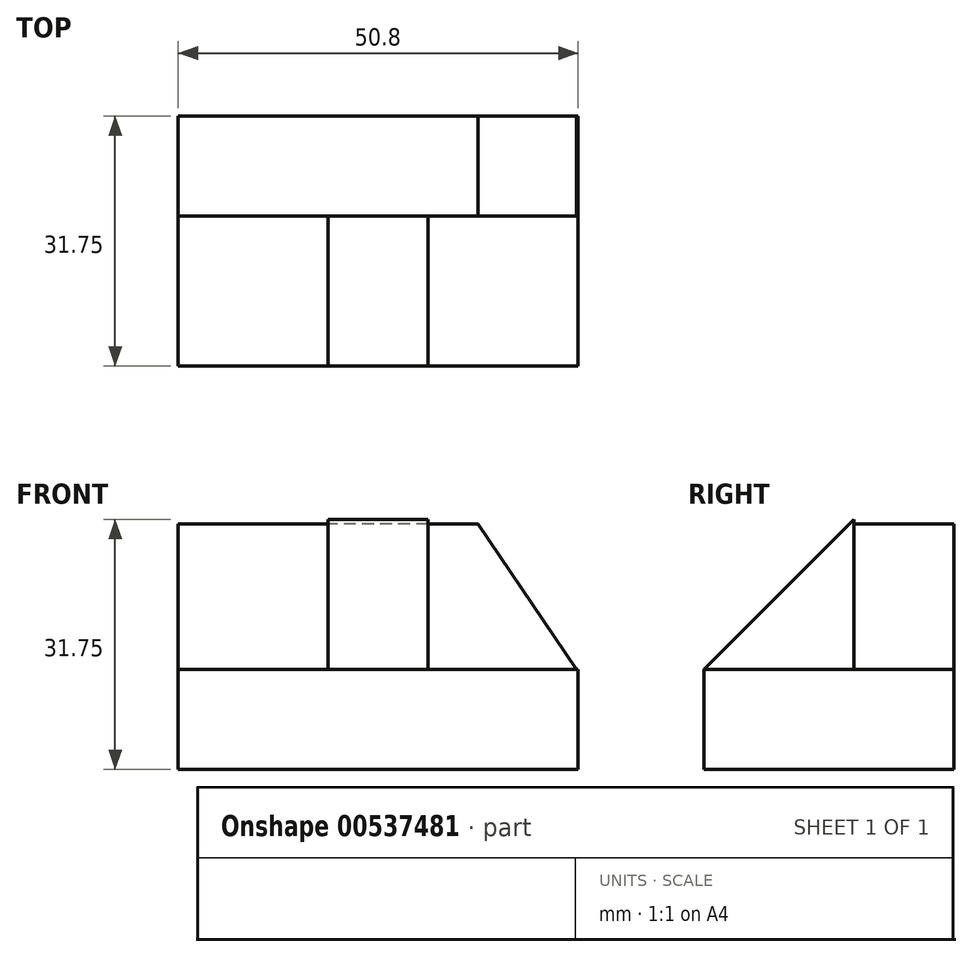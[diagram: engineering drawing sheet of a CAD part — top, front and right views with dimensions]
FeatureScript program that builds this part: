
annotation { "Feature Type Name" : "Feature", "Feature Type Description" : "" }
export const myFeature = defineFeature(function(context is Context, id is Id, definition is map)
    precondition{}
    {
        {
            var Q0;
            Q0=qCreatedBy(makeId("Front.planeOp"),FACE);
            var sketch = newSketch(context, id + "F0", { "sketchPlane" : qUnion([Q0])});
            skLineSegment(sketch, "E0", {"start": v(0, 0) * mm, "end": v(0, 31.75) * mm});
            skLineSegment(sketch, "E1", {"start": v(0, 31.75) * mm, "end": v(38.1, 31.75) * mm});
            skLineSegment(sketch, "E2", {"start": v(38.1, 31.75) * mm, "end": v(50.8, 12.7) * mm});
            skLineSegment(sketch, "E3", {"start": v(50.8, 12.7) * mm, "end": v(50.8, 0) * mm});
            skLineSegment(sketch, "E4", {"start": v(50.8, 0) * mm, "end": v(0, 0) * mm});
            skLineSegment(sketch, "E5", {"start": v(50.8, 12.7) * mm, "end": v(0, 12.7) * mm});
            skLineSegment(sketch, "E6", {"start": v(0, 12.7) * mm, "end": v(0, 0) * mm});
            skSolve(sketch);
        }
        {
            var Q0;
            Q0=makeQuery(id+"F0.imprint","IMPRINT",FACE,{"disambiguationData":[TD([[makeQuery(id+"F0.imprint","IMPRINT",EDGE,{"derivedFrom":sQuery(id+"F0.wireOp",EDGE,"E3")}),-1.0]])]});
            extrude(context, id + "F1", {"entities" : qUnion([Q0]), "depth" : 31.75 * mm, "offsetDistance" : 25.4 * mm});
        }
        {
            var Q0;
            Q0=qCreatedBy(makeId("Front.planeOp"),FACE);
            var sketch = newSketch(context, id + "F2", { "sketchPlane" : qUnion([Q0])});
            skLineSegment(sketch, "E7", {"start": v(50.8, 12.42) * mm, "end": v(38.1, 31.19) * mm});
            skLineSegment(sketch, "E8", {"start": v(38.1, 31.19) * mm, "end": v(0, 31.19) * mm});
            skLineSegment(sketch, "E9", {"start": v(0, 31.19) * mm, "end": v(0, 12.14) * mm});
            skLineSegment(sketch, "E10", {"start": v(0, 12.14) * mm, "end": v(50.8, 12.42) * mm});
            skSolve(sketch);
        }
        {
            var Q0;
            Q0=makeQuery(id+"F2.imprint","IMPRINT",FACE,{"disambiguationData":[TD([[makeQuery(id+"F2.imprint","IMPRINT",EDGE,{"derivedFrom":sQuery(id+"F2.wireOp",EDGE,"E7")}),1.0]])]});
            extrude(context, id + "F3", {"entities" : qUnion([Q0]), "operationType" : NewBodyOperationType.ADD, "depth" : 12.7 * mm, "offsetDistance" : 25.4 * mm});
        }
        {
            var Q0;
            Q0=makeQuery(id+"F1.opExtrude","SWEPT_FACE",FACE,{"disambiguationData":[OSD([sQuery(id+"F0.wireOp",EDGE,"E5")])]});
            var sketch = newSketch(context, id + "F4", { "sketchPlane" : qUnion([Q0])});
            skLineSegment(sketch, "E11", {"start": v(31.75, -12.7) * mm, "end": v(31.75, -31.75) * mm});
            skLineSegment(sketch, "E12", {"start": v(31.75, -31.75) * mm, "end": v(19.05, -31.75) * mm});
            skLineSegment(sketch, "E13", {"start": v(19.05, -31.75) * mm, "end": v(19.05, -12.7) * mm});
            skLineSegment(sketch, "E14", {"start": v(19.05, -12.7) * mm, "end": v(31.75, -12.7) * mm});
            skSolve(sketch);
        }
        {
            var Q0;
            Q0=makeQuery(id+"F4.imprint","IMPRINT",FACE,{"disambiguationData":[TD([[makeQuery(id+"F4.imprint","IMPRINT",EDGE,{"derivedFrom":sQuery(id+"F4.wireOp",EDGE,"E11")}),-1.0]])]});
            extrude(context, id + "F5", {"entities" : qUnion([Q0]), "operationType" : NewBodyOperationType.ADD, "depth" : 19.05 * mm, "offsetDistance" : 25.4 * mm});
        }
        {
            var Q0;
            Q0 = qSketchRegion(id + "F4", true);
            extrude(context, id + "F6", {"entities" : qUnion([Q0]), "operationType" : NewBodyOperationType.ADD, "depth" : 19.05 * mm, "offsetDistance" : 25.4 * mm});
        }
        {
            var Q0;
            Q0=makeQuery(id+"F5.opExtrude","SWEPT_FACE",FACE,{"disambiguationData":[OSD([sQuery(id+"F4.wireOp",EDGE,"E11")])]});
            var sketch = newSketch(context, id + "F7", { "sketchPlane" : qUnion([Q0])});
            skLineSegment(sketch, "E15", {"start": v(-12.7, 31.75) * mm, "end": v(-31.75, 12.7) * mm});
            skLineSegment(sketch, "E16", {"start": v(-31.75, 12.7) * mm, "end": v(-31.75, 31.75) * mm});
            skLineSegment(sketch, "E17", {"start": v(-31.75, 31.75) * mm, "end": v(-12.7, 31.75) * mm});
            skSolve(sketch);
        }
        {
            var Q0;
            Q0=makeQuery(id+"F7.imprint","IMPRINT",FACE,{"disambiguationData":[TD([[makeQuery(id+"F7.imprint","IMPRINT",EDGE,{"derivedFrom":sQuery(id+"F7.wireOp",EDGE,"E15")}),-1.0]])]});
            extrude(context, id + "F8", {"entities" : qUnion([Q0]), "operationType" : NewBodyOperationType.REMOVE, "oppositeDirection" : true, "depth" : 50.8 * mm, "offsetDistance" : 25.4 * mm});
        }
    });
